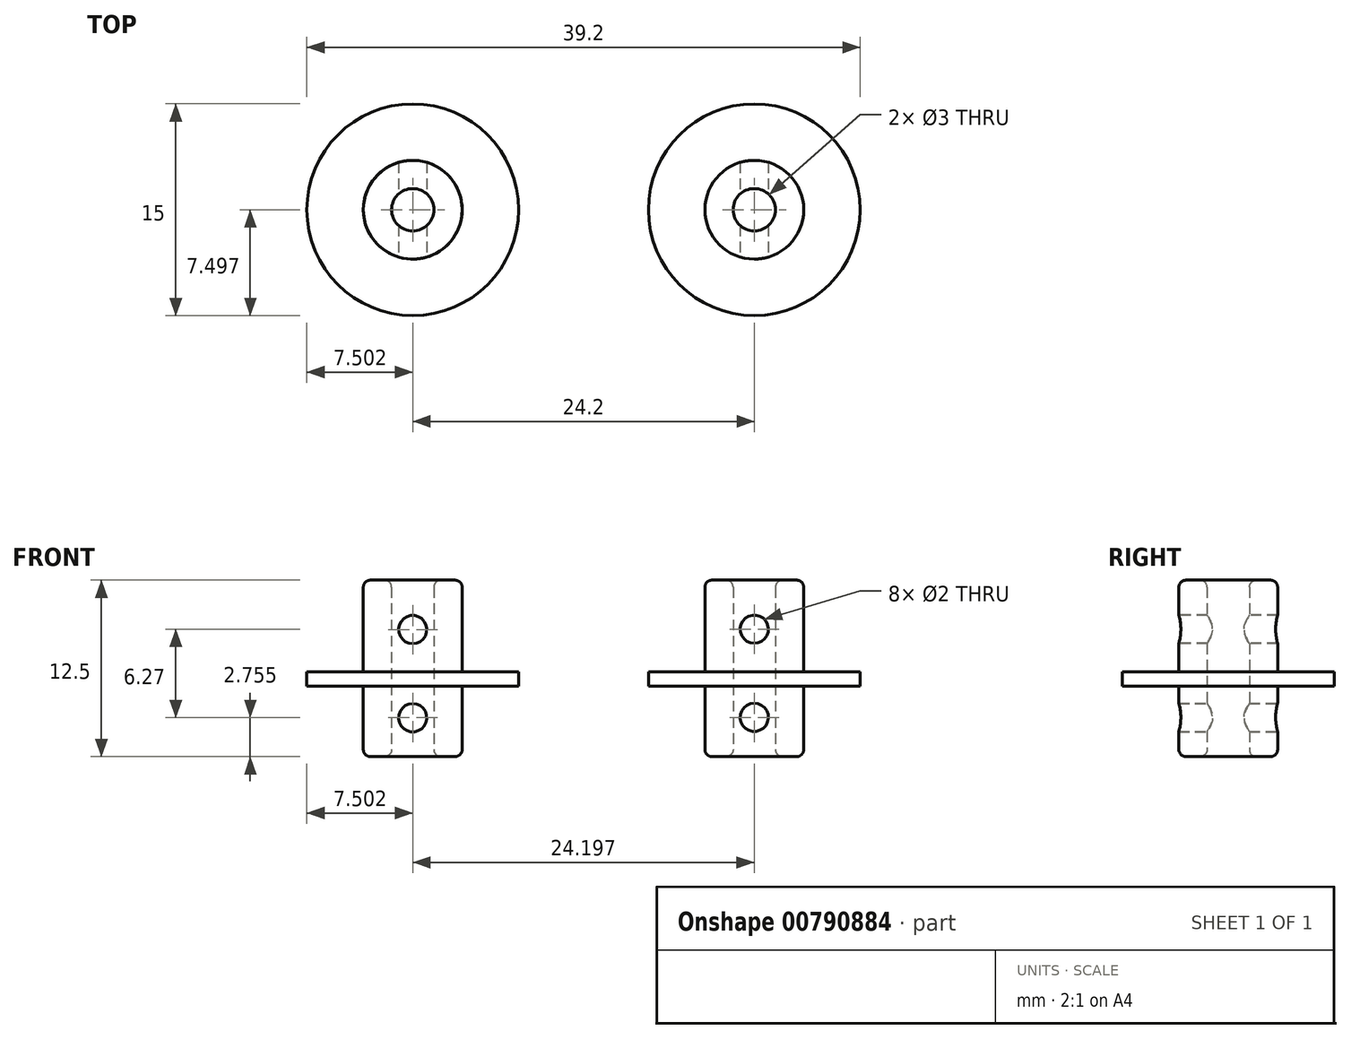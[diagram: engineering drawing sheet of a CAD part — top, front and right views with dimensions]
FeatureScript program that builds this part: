
annotation { "Feature Type Name" : "Feature", "Feature Type Description" : "" }
export const myFeature = defineFeature(function(context is Context, id is Id, definition is map)
    precondition{}
    {
        {
            var Q0;
            Q0=qCreatedBy(makeId("Top.planeOp"),FACE);
            var sketch = newSketch(context, id + "F0", { "sketchPlane" : qUnion([Q0])});
            skCircle(sketch, "E0", {"center": v(-44.45, 33.09) * mm, "radius": 3.5 * mm});
            skCircle(sketch, "E1", {"center": v(-44.45, 33.09) * mm, "radius": 1.5 * mm});
            skSolve(sketch);
        }
        {
            var Q0;
            Q0 = qSketchRegion(id + "F0", true);
            extrude(context, id + "F1", {"entities" : qUnion([Q0]), "depth" : 12.5 * mm, "offsetDistance" : 25 * mm});
        }
        {
            var Q0;
            Q0=makeQuery(id+"F1.opExtrude","CAP_EDGE",EDGE,{"disambiguationData":[OSD([sQuery(id+"F0.wireOp",EDGE,"E0")])],"isStart":false});
            var Q1;
            Q1=makeQuery(id+"F1.opExtrude","CAP_EDGE",EDGE,{"disambiguationData":[OSD([sQuery(id+"F0.wireOp",EDGE,"E0")])],"isStart":true});
            fillet(context, id + "F2", {"entities" : qUnion([Q0, Q1]), "radius" : .5 * mm, "tangentPropagation" : true, "allowEdgeOverflow" : false});
        }
        {
            var Q0;
            Q0=qCreatedBy(makeId("Top.planeOp"),FACE);
            cPlane(context, id + "F3", {"entities" : qUnion([Q0]), "cplaneType" : CPlaneType.OFFSET, "offset" : 5 * mm, "width" : 150 * mm, "height" : 150 * mm});
        }
        {
            var Q0;
            Q0=qCreatedBy(id+"F3.planeOp",FACE);
            var sketch = newSketch(context, id + "F4", { "sketchPlane" : qUnion([Q0])});
            skCircle(sketch, "E2.0", {"center": v(-44.45, 33.09) * mm, "radius": 1.5 * mm});
            skCircle(sketch, "E3", {"center": v(-44.45, 33.09) * mm, "radius": 7.5 * mm});
            skSolve(sketch);
        }
        {
            var Q0;
            Q0 = qSketchRegion(id + "F4", true);
            extrude(context, id + "F5", {"entities" : qUnion([Q0]), "operationType" : NewBodyOperationType.ADD, "depth" : 1 * mm, "offsetDistance" : 25 * mm});
        }
        {
            var Q0;
            Q0=makeQuery(id+"F1.opExtrude","CAP_EDGE",EDGE,{"disambiguationData":[OSD([sQuery(id+"F0.wireOp",EDGE,"E1")])],"isStart":false});
            var Q1;
            Q1=makeQuery(id+"F1.opExtrude","CAP_EDGE",EDGE,{"disambiguationData":[OSD([sQuery(id+"F0.wireOp",EDGE,"E1")])],"isStart":true});
            fillet(context, id + "F6", {"entities" : qUnion([Q0, Q1]), "radius" : .5 * mm, "tangentPropagation" : true, "allowEdgeOverflow" : false});
        }
        {
            var Q0;
            Q0=makeQuery(id+"F1.opExtrude","SWEPT_BODY",BODY,{"disambiguationData":[OSD([sQuery(id+"F0.wireOp",EDGE,"E0"),sQuery(id+"F0.wireOp",EDGE,"E1")])]});
            transform(context, id + "F7", {"entities" : qUnion([Q0]), "transformType" : TransformType.TRANSLATION_3D, "dx" : 24.2 * mm, "dy" : 0 * mm, "dz" : 0 * mm, "makeCopy" : true});
        }
        {
            var Q0;
            Q0=qCreatedBy(makeId("Front.planeOp"),FACE);
            cPlane(context, id + "F8", {"entities" : qUnion([Q0]), "cplaneType" : CPlaneType.OFFSET, "offset" : 33.1 * mm, "oppositeDirection" : true, "width" : 150 * mm, "height" : 150 * mm});
        }
        {
            var Q0;
            Q0=qCreatedBy(id+"F8.planeOp",FACE);
            var sketch = newSketch(context, id + "F9", { "sketchPlane" : qUnion([Q0])});
            skLineSegment(sketch, "E4", {"start": v(-47.95, 6) * mm, "end": v(-47.95, 12) * mm});
            skLineSegment(sketch, "E5", {"start": v(-40.95, 12) * mm, "end": v(-40.95, 6) * mm});
            skLineSegment(sketch, "E6", {"start": v(-47.95, 9) * mm, "end": v(-16.75, 9) * mm, "construction": true});
            skLineSegment(sketch, "E7", {"start": v(-47.95, 12) * mm, "end": v(-40.95, 12) * mm, "construction": true});
            skLineSegment(sketch, "E8", {"start": v(-44.45, 12) * mm, "end": v(-44.45, 6) * mm, "construction": true});
            skCircle(sketch, "E9", {"center": v(-44.45, 9) * mm, "radius": 1 * mm});
            skLineSegment(sketch, "E10", {"start": v(-16.75, 12.03) * mm, "end": v(-23.78, 12.03) * mm, "construction": true});
            skLineSegment(sketch, "E11", {"start": v(-23.78, 12.03) * mm, "end": v(-20.26, 12.03) * mm, "construction": true});
            skLineSegment(sketch, "E12", {"start": v(-20.26, 12.03) * mm, "end": v(-20.26, 6.08) * mm, "construction": true});
            skCircle(sketch, "E13", {"center": v(-20.25, 9.03) * mm, "radius": 1 * mm});
            skSolve(sketch);
        }
        {
            var Q0;
            Q0 = qSketchRegion(id + "F9", true);
            extrude(context, id + "F10", {"entities" : qUnion([Q0]), "operationType" : NewBodyOperationType.REMOVE, "oppositeDirection" : true, "depth" : 4 * mm, "offsetDistance" : 25 * mm, "hasSecondDirection" : true, "secondDirectionOppositeDirection" : false, "secondDirectionDepth" : 4.2 * mm});
        }
        {
            var Q0;
            Q0=qCreatedBy(id+"F8.planeOp",FACE);
            var sketch = newSketch(context, id + "F11", { "sketchPlane" : qUnion([Q0])});
            skLineSegment(sketch, "E14", {"start": v(-47.95, 5.02) * mm, "end": v(-47.95, 0.51) * mm, "construction": true});
            skLineSegment(sketch, "E15", {"start": v(-47.95, 2.76) * mm, "end": v(-16.74, 2.76) * mm, "construction": true});
            skLineSegment(sketch, "E16", {"start": v(-40.94, 5.01) * mm, "end": v(-40.94, 0.51) * mm, "construction": true});
            skCircle(sketch, "E17.0", {"center": v(-44.45, 9) * mm, "radius": 1 * mm, "construction": true});
            skLineSegment(sketch, "E18", {"start": v(-44.45, 9) * mm, "end": v(-44.45, 0.54) * mm, "construction": true});
            skCircle(sketch, "E19.0", {"center": v(-20.25, 9.03) * mm, "radius": 1 * mm});
            skLineSegment(sketch, "E20", {"start": v(-20.25, 9.03) * mm, "end": v(-20.25, 0.54) * mm, "construction": true});
            skLineSegment(sketch, "E21", {"start": v(-47.95, -0.24) * mm, "end": v(-47.95, 5.76) * mm});
            skLineSegment(sketch, "E22", {"start": v(-40.95, 5.76) * mm, "end": v(-40.95, -0.24) * mm});
            skLineSegment(sketch, "E23", {"start": v(-47.95, 2.76) * mm, "end": v(-16.75, 2.76) * mm, "construction": true});
            skLineSegment(sketch, "E24", {"start": v(-47.95, 5.76) * mm, "end": v(-40.95, 5.76) * mm, "construction": true});
            skLineSegment(sketch, "E25", {"start": v(-44.45, 5.76) * mm, "end": v(-44.45, -0.25) * mm, "construction": true});
            skCircle(sketch, "E26", {"center": v(-44.45, 2.76) * mm, "radius": 1 * mm});
            skLineSegment(sketch, "E27", {"start": v(-16.75, 5.78) * mm, "end": v(-23.78, 5.78) * mm, "construction": true});
            skLineSegment(sketch, "E28", {"start": v(-23.78, 5.78) * mm, "end": v(-20.26, 5.78) * mm, "construction": true});
            skLineSegment(sketch, "E29", {"start": v(-20.26, 5.78) * mm, "end": v(-20.26, -0.17) * mm, "construction": true});
            skCircle(sketch, "E30", {"center": v(-20.25, 2.78) * mm, "radius": 1 * mm});
            skSolve(sketch);
        }
        {
            var Q0;
            Q0 = qSketchRegion(id + "F11", true);
            extrude(context, id + "F12", {"entities" : qUnion([Q0]), "operationType" : NewBodyOperationType.REMOVE, "depth" : 7 * mm, "offsetDistance" : 25 * mm, "hasSecondDirection" : true, "secondDirectionOppositeDirection" : true, "secondDirectionDepth" : 7 * mm});
        }
    });
